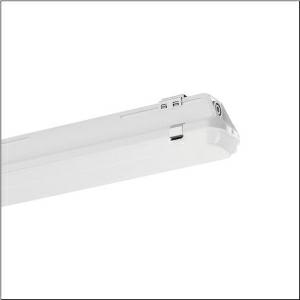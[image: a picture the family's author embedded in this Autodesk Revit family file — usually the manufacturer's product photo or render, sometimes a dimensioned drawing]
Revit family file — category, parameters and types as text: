
# Revit family: monsun_r__11_51fp20mp4b0u_7a3b
name_source: partatom
category: Lighting Fixtures
units: mm (PartAtom-declared; Revit-internal decimal feet)

## family parameters
Cut with Voids When Loaded = No
Host = Face
Light Source = No
Part Type = Normal
Room Calculation Point = No
Round Connector Dimension = Use Diameter
Shared = No

## types (1)
- --- (1 x LED, 10910 lm, 62.4 W, 4000K)
    Apparent Load = 62 VA
    CIE Flux Codes = 45 75 93 94 100
    Color Rendering = 80
    Color Temperature = 4000K
    Default Elevation = 1800 mm
    Description = Monsun® 11, damp-proof luminaire, chain hanger, primary optical cover: enclosure, of PC, light emission: direct distribution, primary light characteristic: symmetric, installation type: suspended mounting, surface-mounted, horizontal mounting, vertical mounting, LED, rated luminous flux: 10.910lm, luminous efficacy: 175lm/W, light colour: 840, colour temperature: 4000K, control gear: ON/OFF Multilumen, with terminal, 3-pole, max. 2.5mm², mains connection: 220..240V, AC, 50/60Hz, rated input power: 62W, luminaire housing, of glass-fibre reinforced polyester, uncoated, bright grey, incl. chain hanger, length: 1.590mm, width: 90mm, height: 88mm, clip for enclosure, of stainless steel (V2A), ceiling mounting element, of stainless steel (V2A), chain hanger, of stainless steel (V2A), protection rating (complete): IP66, insulation class (complete): insulation class I (protective earthing), certification: CE, ENEC, VDE, UKCA, protection symbol: D, impact resistance: IK08, permissible operating ambient temperature: -35..+35°C, standard: EN 50419, EN 60598-2-1, contact your sales advisor before using the luminaires in applications with unclear chemical exposure, large temperature fluctuations or condensation-forming humidity, LABS conformity tested according to VDMA 24364:2018-05, no direct snow, no direct sun, no direct rain, for indoor or canopied outdoor use, corresponds to IFS (International Featured Standards) requirements for safety and quality in the food industry, packaging unit: 1 piece
    Height = 89 mm
    Lamp = 1 x LED
    Lamp Light Flux = 10910 lm
    Lamp Power = 62.4 W
    Lamp count = 1
    Length = 1590 mm
    Luminous efficacy = 175 lm/W
    Manufacturer = Siteco
    ModVariant = No
    Model = 51FP20MP4B0U
    Mounting Place = Ceiling
    Mounting Type = Surface mounted
    Number of Poles = 1
    OnlyDefault = Yes
    Power Factor = 1
    Product Name = Monsun® 11
    Product group = damp-proof luminaire
    ProductGroupID = 300
    Protection Class = Protection class I
    Protection Degree = IP 66
    RLX_Detail_Level = 1
    RLX_Emergency_Light_Flux = 0 lm
    RLX_Emergency_Type = 0
    RLX_Emergency_Type_DB = No
    RlxData = <blob elided: 89757 chars, md5=681fa112>
    Socket = socket
    Standby Power = 0 W
    System Light Flux = 10910 lm
    System Power = 62 W
    Type Comments = factory setting: luminous flux: 100 % | (A | C | E) | 147 mA
    Type Image = l_1349237.jpg
    URL = http://relux.com
    VarID = @adj_021166
    Voltage = 0 V
    Weight = 0.00 kg
    Width = 90 mm

## geometry (parser evidence)
native form markers: Blend x4, Sweep x14
no freeform markers — native parametric forms only
